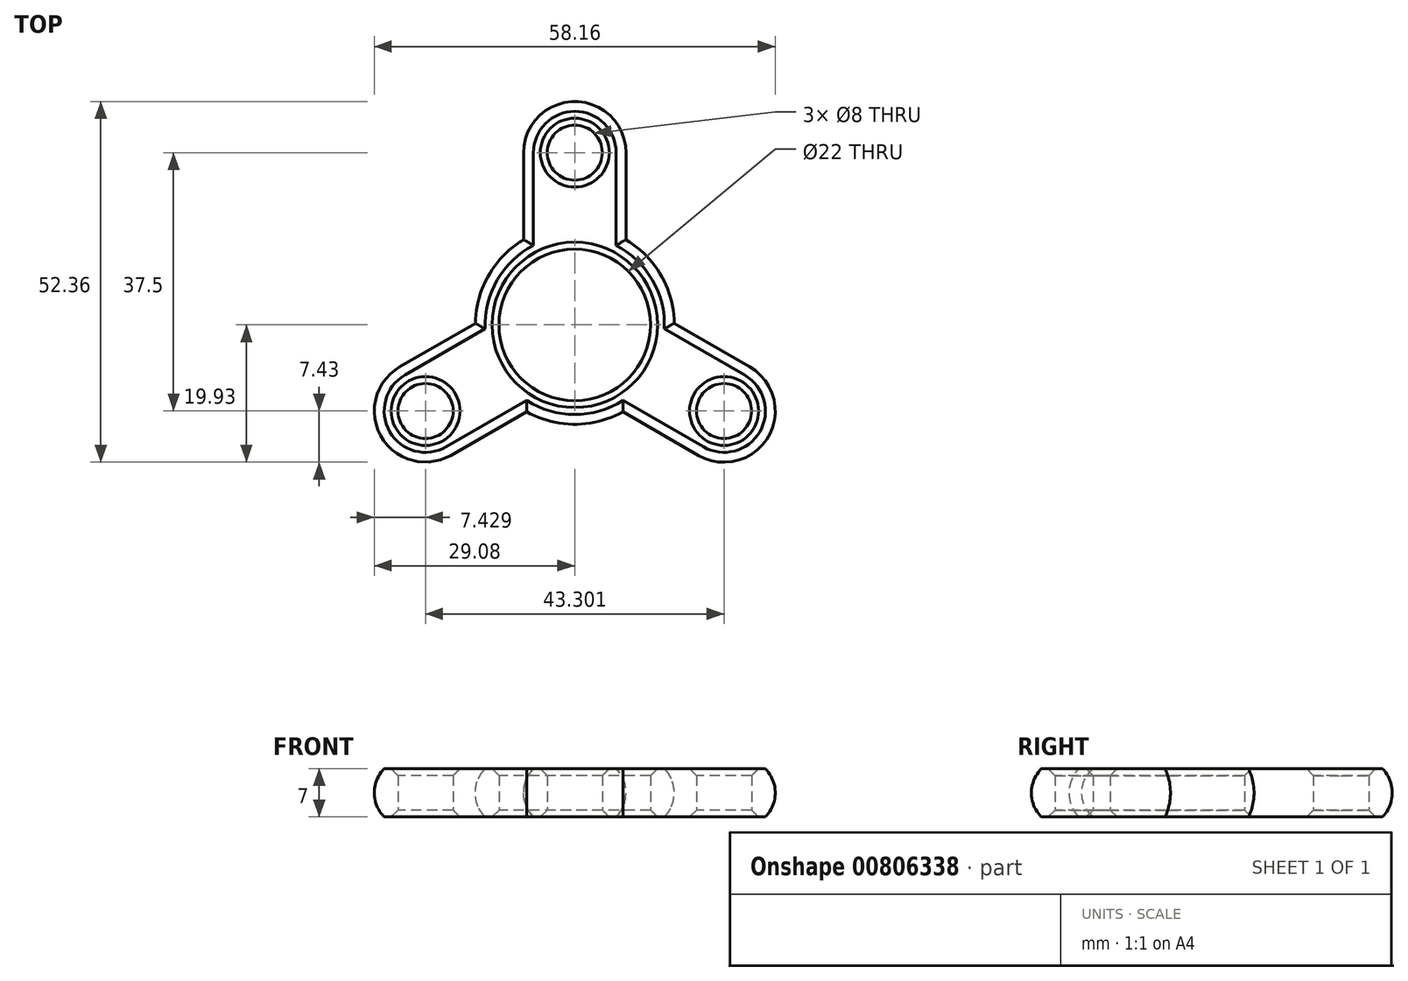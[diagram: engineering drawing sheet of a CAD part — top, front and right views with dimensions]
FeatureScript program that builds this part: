
annotation { "Feature Type Name" : "Feature", "Feature Type Description" : "" }
export const myFeature = defineFeature(function(context is Context, id is Id, definition is map)
    precondition{}
    {
        {
            var Q0;
            Q0=qCreatedBy(makeId("Top.planeOp"),FACE);
            var sketch = newSketch(context, id + "F0", { "sketchPlane" : qUnion([Q0])});
            skCircle(sketch, "E0", {"center": v(0, 0) * mm, "radius": 11 * mm});
            skCircle(sketch, "E1", {"center": v(0, 0) * mm, "radius": 13 * mm});
            skCircle(sketch, "E2", {"center": v(0, 25) * mm, "radius": 4 * mm});
            skCircle(sketch, "E3", {"center": v(0, 25) * mm, "radius": 6 * mm});
            skPoint(sketch, "E4.center", {"position": v(0, 0.5) * mm});
            skCircle(sketch, "E5.1.0", {"center": v(-21.65, -12.5) * mm, "radius": 6 * mm});
            skCircle(sketch, "E5.1.1", {"center": v(-21.65, -12.5) * mm, "radius": 4 * mm});
            skCircle(sketch, "E5.2.0", {"center": v(21.65, -12.5) * mm, "radius": 6 * mm});
            skCircle(sketch, "E5.2.1", {"center": v(21.65, -12.5) * mm, "radius": 4 * mm});
            skLineSegment(sketch, "E6", {"start": v(-6, 25) * mm, "end": v(-6, 11.53) * mm});
            skLineSegment(sketch, "E7", {"start": v(6, 25) * mm, "end": v(6, 11.53) * mm});
            skLineSegment(sketch, "E8.1.0", {"start": v(-18.65, -17.7) * mm, "end": v(-6.99, -10.96) * mm});
            skLineSegment(sketch, "E8.1.1", {"start": v(-24.65, -7.3) * mm, "end": v(-12.99, -0.57) * mm});
            skLineSegment(sketch, "E8.2.0", {"start": v(24.65, -7.3) * mm, "end": v(12.99, -0.57) * mm});
            skLineSegment(sketch, "E8.2.1", {"start": v(18.65, -17.7) * mm, "end": v(6.99, -10.96) * mm});
            skSolve(sketch);
        }
        {
            var Q0;
            Q0=makeQuery(id+"F0.imprint","IMPRINT",FACE,{"disambiguationData":[TD([[makeQuery(id+"F0.imprint","IMPRINT",EDGE,{"derivedFrom":sQuery(id+"F0.wireOp",EDGE,"E1")}),-1.0]])]});
            var Q1;
            Q1=makeQuery(id+"F0.imprint","IMPRINT",FACE,{"disambiguationData":[TD([[makeQuery(id+"F0.imprint","IMPRINT",EDGE,{"derivedFrom":sQuery(id+"F0.wireOp",EDGE,"c202e4ac-ae93-4b29-baa2-4fd0cf997ff0.1.0")}),-1.0]])]});
            var Q2;
            Q2=makeQuery(id+"F0.imprint","IMPRINT",FACE,{"disambiguationData":[TD([[makeQuery(id+"F0.imprint","IMPRINT",EDGE,{"derivedFrom":sQuery(id+"F0.wireOp",EDGE,"E0")}),-1.0]])]});
            var Q3;
            Q3=makeQuery(id+"F0.imprint","IMPRINT",FACE,{"disambiguationData":[TD([[makeQuery(id+"F0.imprint","IMPRINT",EDGE,{"derivedFrom":sQuery(id+"F0.wireOp",EDGE,"E2")}),-1.0]])]});
            var Q4;
            Q4=makeQuery(id+"F0.imprint","IMPRINT",FACE,{"disambiguationData":[TD([[makeQuery(id+"F0.imprint","IMPRINT",EDGE,{"derivedFrom":sQuery(id+"F0.wireOp",EDGE,"c202e4ac-ae93-4b29-baa2-4fd0cf997ff0.2.0")}),-1.0]])]});
            var Q5;
            Q5=makeQuery(id+"F0.imprint","IMPRINT",FACE,{"disambiguationData":[TD([[makeQuery(id+"F0.imprint","IMPRINT",EDGE,{"derivedFrom":sQuery(id+"F0.wireOp",EDGE,"0e0c9052-6751-44d5-bc73-aae295e7aca2.2.0")}),-1.0]])]});
            var Q6;
            Q6=makeQuery(id+"F0.imprint","IMPRINT",FACE,{"disambiguationData":[TD([[makeQuery(id+"F0.imprint","IMPRINT",EDGE,{"derivedFrom":sQuery(id+"F0.wireOp",EDGE,"0e0c9052-6751-44d5-bc73-aae295e7aca2.4.0")}),-1.0]])]});
            var Q7;
            Q7=makeQuery(id+"F0.imprint","IMPRINT",FACE,{"disambiguationData":[TD([[makeQuery(id+"F0.imprint","IMPRINT",EDGE,{"derivedFrom":sQuery(id+"F0.wireOp",EDGE,"6d77e2d1-ec52-477d-ae8a-bde1fbb15b47.4.1")}),-1.0]])]});
            var Q8;
            Q8=makeQuery(id+"F0.imprint","IMPRINT",FACE,{"disambiguationData":[TD([[makeQuery(id+"F0.imprint","IMPRINT",EDGE,{"derivedFrom":sQuery(id+"F0.wireOp",EDGE,"6d77e2d1-ec52-477d-ae8a-bde1fbb15b47.2.1")}),-1.0]])]});
            var Q9;
            Q9=makeQuery(id+"F0.imprint","IMPRINT",FACE,{"disambiguationData":[TD([[makeQuery(id+"F0.imprint","IMPRINT",EDGE,{"derivedFrom":sQuery(id+"F0.wireOp",EDGE,"3cc0715d-66bc-4789-9b96-2980e166defb.4.1")}),-1.0]])]});
            var Q10;
            Q10=makeQuery(id+"F0.imprint","IMPRINT",FACE,{"disambiguationData":[TD([[makeQuery(id+"F0.imprint","IMPRINT",EDGE,{"derivedFrom":sQuery(id+"F0.wireOp",EDGE,"3cc0715d-66bc-4789-9b96-2980e166defb.2.1")}),-1.0]])]});
            var Q11;
            Q11=makeQuery(id+"F0.imprint","IMPRINT",FACE,{"disambiguationData":[TD([[makeQuery(id+"F0.imprint","IMPRINT",EDGE,{"derivedFrom":sQuery(id+"F0.wireOp",EDGE,"E5.1.1")}),-1.0]])]});
            var Q12;
            Q12=makeQuery(id+"F0.imprint","IMPRINT",FACE,{"disambiguationData":[TD([[makeQuery(id+"F0.imprint","IMPRINT",EDGE,{"derivedFrom":sQuery(id+"F0.wireOp",EDGE,"E5.2.1")}),-1.0]])]});
            extrude(context, id + "F1", {"entities" : qUnion([Q0, Q1, Q2, Q3, Q4, Q5, Q6, Q7, Q8, Q9, Q10, Q11, Q12]), "endBound" : BoundingType.SYMMETRIC, "depth" : 7 * mm, "offsetDistance" : 25.4 * mm});
        }
        {
            var Q0;
            Q0=qCreatedBy(makeId("Right.planeOp"),FACE);
            var sketch = newSketch(context, id + "F2", { "sketchPlane" : qUnion([Q0])});
            skLineSegment(sketch, "E9", {"start": v(31, 3.5) * mm, "end": v(31, -3.5) * mm});
            skArc(sketch, "E10", {"start": v(31, -3.5) * mm, "mid": v(32.43, 0) * mm, "end": v(31, 3.5) * mm});
            skSolve(sketch);
        }
        {
            var Q0;
            Q0=makeQuery(id+"F2.imprint","IMPRINT",FACE,{"disambiguationData":[TD([[makeQuery(id+"F2.imprint","IMPRINT",EDGE,{"derivedFrom":sQuery(id+"F2.wireOp",EDGE,"E9")}),1.0]])]});
            var Q1;
            Q1=makeQuery(id+"F1.opExtrude","CAP_EDGE",EDGE,{"disambiguationData":[OSD([sQuery(id+"F0.wireOp",EDGE,"E3")])],"isStart":false});
            var Q2;
            Q2=makeQuery(id+"F1.opExtrude","CAP_EDGE",EDGE,{"disambiguationData":[OSD([sQuery(id+"F0.wireOp",EDGE,"E7")])],"isStart":false});
            var Q3;
            {var subQ0=sQuery(id+"F0.wireOp",EDGE,"E1");Q3=makeQuery(id+"F1.opExtrude","CAP_EDGE",EDGE,{"disambiguationData":[OSD([subQ0]),TDD([makeQuery(id+"F0.imprint","IMPRINT",EDGE,{"disambiguationData":[TD([[makeQuery(id+"F0.imprint","INTERSECT",VERTEX,{"derivedFrom":[subQ0,sQuery(id+"F0.wireOp",EDGE,"E7")]}),1.0]])],"derivedFrom":subQ0})])],"isStart":false});}
            var Q4;
            Q4=makeQuery(id+"F1.opExtrude","CAP_EDGE",EDGE,{"disambiguationData":[OSD([sQuery(id+"F0.wireOp",EDGE,"E8.2.0")])],"isStart":false});
            var Q5;
            Q5=makeQuery(id+"F1.opExtrude","CAP_EDGE",EDGE,{"disambiguationData":[OSD([sQuery(id+"F0.wireOp",EDGE,"E5.2.0")])],"isStart":false});
            var Q6;
            Q6=makeQuery(id+"F1.opExtrude","CAP_EDGE",EDGE,{"disambiguationData":[OSD([sQuery(id+"F0.wireOp",EDGE,"E8.2.1")])],"isStart":false});
            var Q7;
            {var subQ0=sQuery(id+"F0.wireOp",EDGE,"E1");Q7=makeQuery(id+"F1.opExtrude","CAP_EDGE",EDGE,{"disambiguationData":[OSD([subQ0]),TDD([makeQuery(id+"F0.imprint","IMPRINT",EDGE,{"disambiguationData":[TD([[makeQuery(id+"F0.imprint","INTERSECT",VERTEX,{"derivedFrom":[subQ0,sQuery(id+"F0.wireOp",EDGE,"E8.1.0")]}),-1.0]])],"derivedFrom":subQ0})])],"isStart":false});}
            var Q8;
            Q8=makeQuery(id+"F1.opExtrude","CAP_EDGE",EDGE,{"disambiguationData":[OSD([sQuery(id+"F0.wireOp",EDGE,"E8.1.0")])],"isStart":false});
            var Q9;
            Q9=makeQuery(id+"F1.opExtrude","CAP_EDGE",EDGE,{"disambiguationData":[OSD([sQuery(id+"F0.wireOp",EDGE,"E5.1.0")])],"isStart":false});
            var Q10;
            Q10=makeQuery(id+"F1.opExtrude","CAP_EDGE",EDGE,{"disambiguationData":[OSD([sQuery(id+"F0.wireOp",EDGE,"E8.1.1")])],"isStart":false});
            var Q11;
            {var subQ0=sQuery(id+"F0.wireOp",EDGE,"E1");Q11=makeQuery(id+"F1.opExtrude","CAP_EDGE",EDGE,{"disambiguationData":[OSD([subQ0]),TDD([makeQuery(id+"F0.imprint","IMPRINT",EDGE,{"disambiguationData":[TD([[makeQuery(id+"F0.imprint","INTERSECT",VERTEX,{"derivedFrom":[subQ0,sQuery(id+"F0.wireOp",EDGE,"E6")]}),-1.0]])],"derivedFrom":subQ0})])],"isStart":false});}
            var Q12;
            Q12=makeQuery(id+"F1.opExtrude","CAP_EDGE",EDGE,{"disambiguationData":[OSD([sQuery(id+"F0.wireOp",EDGE,"E6")])],"isStart":false});
            sweep(context, id + "F3", {"operationType" : NewBodyOperationType.ADD, "profiles" : qUnion([Q0]), "path" : qUnion([Q1, Q2, Q3, Q4, Q5, Q6, Q7, Q8, Q9, Q10, Q11, Q12])});
        }
        {
            var Q0;
            Q0=makeQuery(id+"F1.opExtrude","CAP_EDGE",EDGE,{"disambiguationData":[OSD([sQuery(id+"F0.wireOp",EDGE,"E2")])],"isStart":false});
            var Q1;
            Q1=makeQuery(id+"F1.opExtrude","CAP_EDGE",EDGE,{"disambiguationData":[OSD([sQuery(id+"F0.wireOp",EDGE,"E0")])],"isStart":false});
            var Q2;
            Q2=makeQuery(id+"F1.opExtrude","CAP_EDGE",EDGE,{"disambiguationData":[OSD([sQuery(id+"F0.wireOp",EDGE,"E5.1.1")])],"isStart":false});
            var Q3;
            Q3=makeQuery(id+"F1.opExtrude","CAP_EDGE",EDGE,{"disambiguationData":[OSD([sQuery(id+"F0.wireOp",EDGE,"E5.2.1")])],"isStart":false});
            var Q4;
            Q4=makeQuery(id+"F1.opExtrude","CAP_EDGE",EDGE,{"disambiguationData":[OSD([sQuery(id+"F0.wireOp",EDGE,"E5.1.1")])],"isStart":true});
            var Q5;
            Q5=makeQuery(id+"F1.opExtrude","CAP_EDGE",EDGE,{"disambiguationData":[OSD([sQuery(id+"F0.wireOp",EDGE,"E0")])],"isStart":true});
            var Q6;
            Q6=makeQuery(id+"F1.opExtrude","CAP_EDGE",EDGE,{"disambiguationData":[OSD([sQuery(id+"F0.wireOp",EDGE,"E5.2.1")])],"isStart":true});
            var Q7;
            Q7=makeQuery(id+"F1.opExtrude","CAP_EDGE",EDGE,{"disambiguationData":[OSD([sQuery(id+"F0.wireOp",EDGE,"E2")])],"isStart":true});
            chamfer(context, id + "F4", {"entities" : qUnion([Q0, Q1, Q2, Q3, Q4, Q5, Q6, Q7]), "width" : 1 * mm, "tangentPropagation" : true});
        }
    });
